# Revit family: Electrical_Equipment-Floor_Box-Hubbell_Wiring-1_Gang-Rectangular_Stamped_Steel-B2429
name_source: partatom
category: Electrical Fixtures
revit_build: Autodesk Revit 2015 (Build: 20140606_1530(x64)
units: mm (PartAtom-declared; Revit-internal decimal feet)

## types (1)
- B2429 - 1 Gang - Brass Collar
    Assembly Code = D5020115
    Box Material = Metal-Hubbell-Stamped Steel
    Collar Material = Metal-Hubbell-Brass
    Conduit Connector 1 Radius = 0' - 0 1/4"
    Conduit Connector 2 Radius = 0' - 0 3/8"
    Conduit Connector_1 Description = Conduit 0.5in. Connection
    Conduit Connector_10 Description = Conduit 0.75in. Connection
    Conduit Connector_11 Description = Conduit 0.5in. Connection
    Conduit Connector_12 Description = Conduit 0.5in. Connection
    Conduit Connector_13 Description = Conduit 0.5in. Connection
    Conduit Connector_14 Description = Conduit 0.75in. Connection
    Conduit Connector_15 Description = Conduit 0.75in. Connection
    Conduit Connector_2 Description = Conduit 0.75in. Connection
    Conduit Connector_3 Description = Conduit 0.5in. Connection
    Conduit Connector_4 Description = Conduit 0.75in. Connection
    Conduit Connector_5 Description = Conduit 0.5in. Connection
    Conduit Connector_6 Description = Conduit 0.5in. Connection
    Conduit Connector_7 Description = Conduit 0.75in. Connection
    Conduit Connector_8 Description = Conduit 0.5in. Connection
    Conduit Connector_9 Description = Conduit 0.5in. Connection
    Default Elevation = 0' - 0"
    Description = Flush Rectangular Stamped Steel Concrete Floor Box
    Floor Box Type = Stamped Steel Concrete Floor Box : B2429 - Shallow Concrete Floor Box
    Manufacturer = Hubbell-Wiring
    Model = B2429
    Product Documentation Link = http://ecatalog.hubbell-wiring.com
    Product Page URL = http://ecatalog.hubbell-wiring.com
    Product data url = https://bimobject.com
    URL = http://www.hubbell-wiring.com

## geometry (parser evidence)
native form markers: Blend x21, Sweep x6
no freeform markers — native parametric forms only
